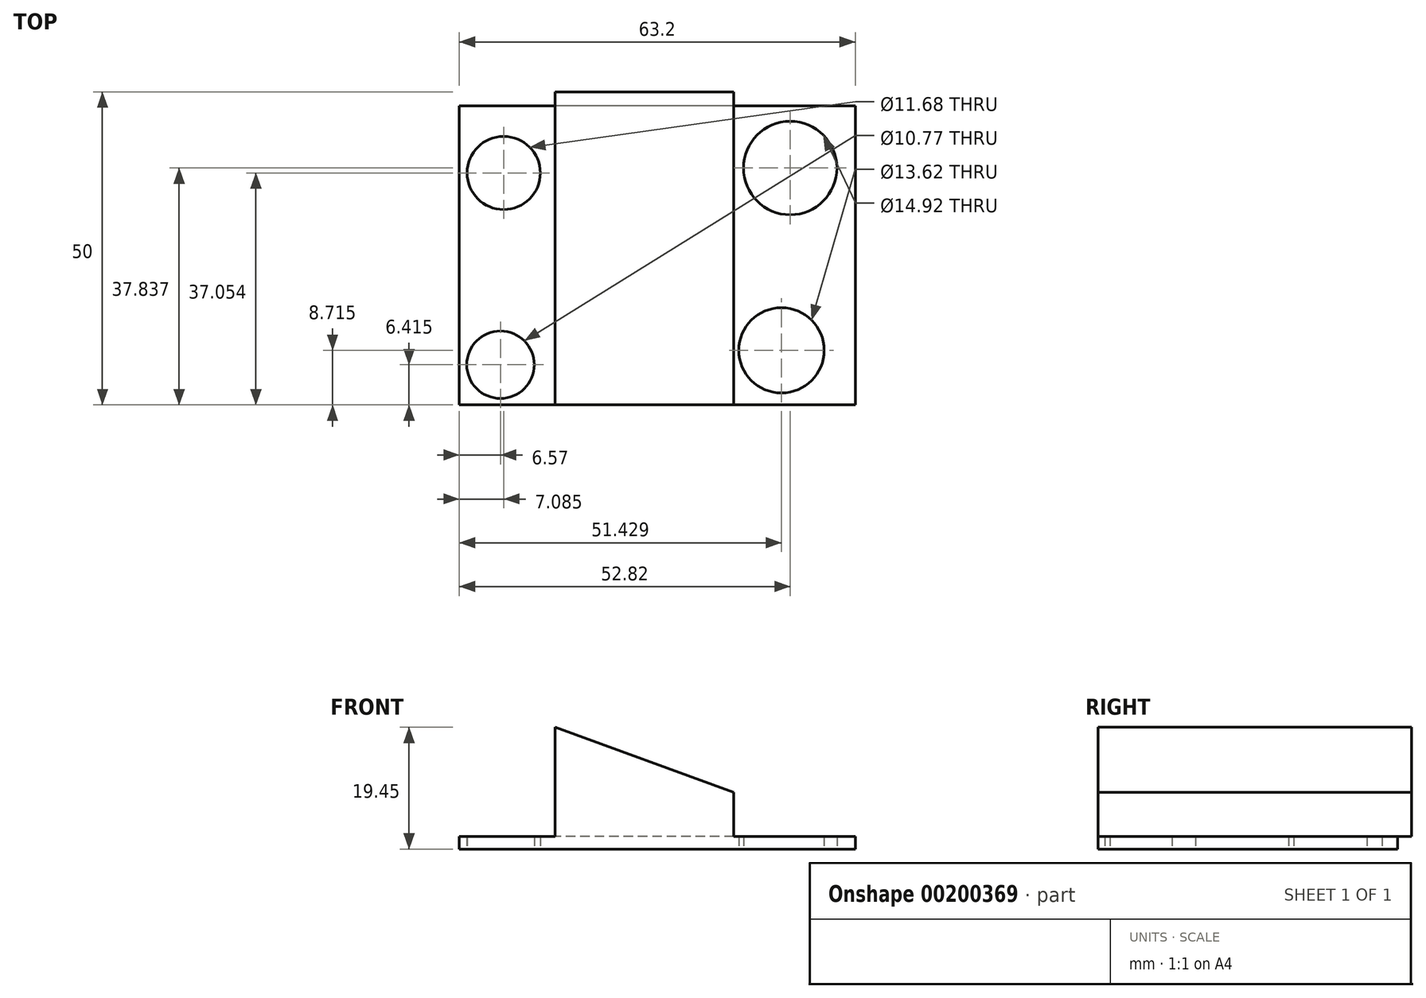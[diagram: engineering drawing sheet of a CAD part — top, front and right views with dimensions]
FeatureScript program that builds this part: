
annotation { "Feature Type Name" : "Feature", "Feature Type Description" : "" }
export const myFeature = defineFeature(function(context is Context, id is Id, definition is map)
    precondition{}
    {
        {
            var Q0;
            Q0=qCreatedBy(makeId("Top.planeOp"),FACE);
            var sketch = newSketch(context, id + "F0", { "sketchPlane" : qUnion([Q0])});
            skLineSegment(sketch, "E0.bottom", {"start": v(31.6, -23.9) * mm, "end": v(-31.6, -23.9) * mm});
            skLineSegment(sketch, "E0.top", {"start": v(31.6, 23.9) * mm, "end": v(-31.6, 23.9) * mm});
            skLineSegment(sketch, "E0.left", {"start": v(31.6, -23.9) * mm, "end": v(31.6, 23.9) * mm});
            skLineSegment(sketch, "E0.right", {"start": v(-31.6, -23.9) * mm, "end": v(-31.6, 23.9) * mm});
            skPoint(sketch, "E0.middle", {"position": v(0, 0) * mm});
            skCircle(sketch, "E1", {"center": v(-24.51, 13.15) * mm, "radius": 5.84 * mm});
            skCircle(sketch, "E2", {"center": v(-25.03, -17.49) * mm, "radius": 5.38 * mm});
            skCircle(sketch, "E3", {"center": v(19.83, -15.19) * mm, "radius": 6.8 * mm});
            skCircle(sketch, "E4", {"center": v(21.22, 13.94) * mm, "radius": 7.46 * mm});
            skSolve(sketch);
        }
        {
            var Q0;
            Q0=makeQuery(id+"F0.imprint","IMPRINT",FACE,{"disambiguationData":[TD([[makeQuery(id+"F0.imprint","IMPRINT",EDGE,{"derivedFrom":sQuery(id+"F0.wireOp",EDGE,"E0.bottom")}),-1.0]])]});
            extrude(context, id + "F1", {"entities" : qUnion([Q0]), "depth" : 2 * mm});
        }
        {
            var Q0;
            Q0=makeQuery(id+"F1.opExtrude","SWEPT_FACE",FACE,{"disambiguationData":[OSD([sQuery(id+"F0.wireOp",EDGE,"E0.bottom")])]});
            var sketch = newSketch(context, id + "F2", { "sketchPlane" : qUnion([Q0])});
            skLineSegment(sketch, "E5", {"start": v(31.6, 2) * mm, "end": v(-27.73, 23.6) * mm});
            skLineSegment(sketch, "E6", {"start": v(-27.73, 23.6) * mm, "end": v(-31.6, 2) * mm});
            skLineSegment(sketch, "E7", {"start": v(-16.34, 2) * mm, "end": v(-16.34, 19.45) * mm});
            skLineSegment(sketch, "E8", {"start": v(12.22, 2) * mm, "end": v(12.22, 9.06) * mm});
            skSolve(sketch);
        }
        {
            var Q0;
            {var subQ0=sQuery(id+"F2.wireOp",EDGE,"E7");Q0=makeQuery(id+"F2.imprint","IMPRINT",FACE,{"disambiguationData":[TD([[makeQuery(id+"F2.imprint","IMPRINT",EDGE,{"derivedFrom":subQ0}),-1.0]])]});}
            extrude(context, id + "F3", {"entities" : qUnion([Q0]), "operationType" : NewBodyOperationType.ADD, "oppositeDirection" : true, "depth" : 50 * mm});
        }
    });
